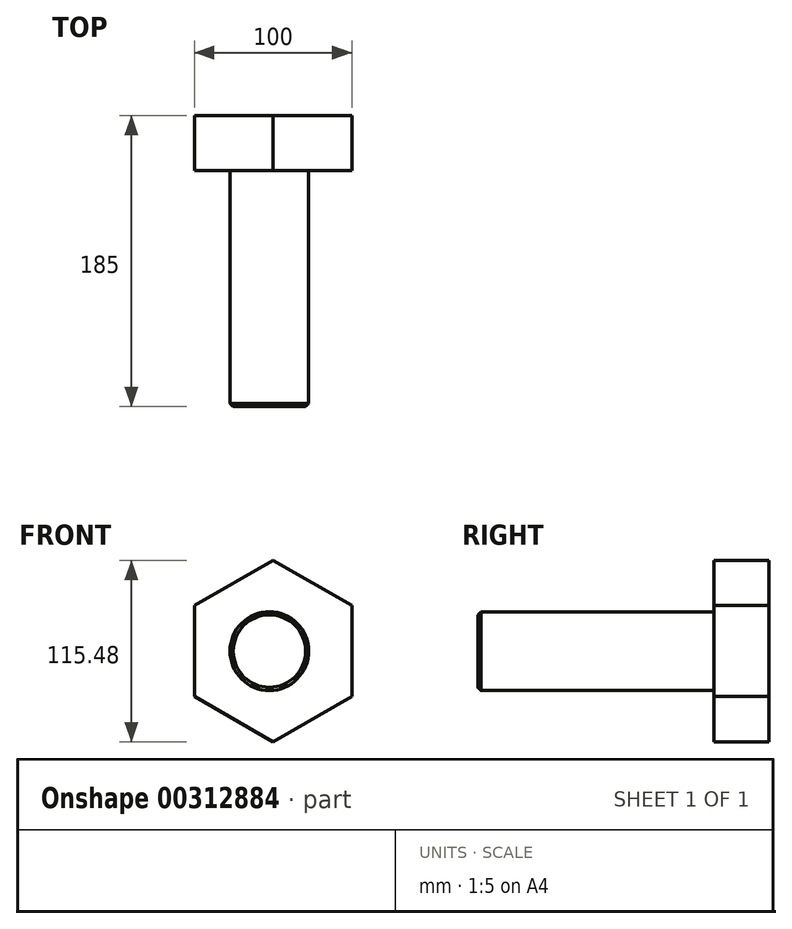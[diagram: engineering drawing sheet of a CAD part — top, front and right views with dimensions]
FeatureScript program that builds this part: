
annotation { "Feature Type Name" : "Feature", "Feature Type Description" : "" }
export const myFeature = defineFeature(function(context is Context, id is Id, definition is map)
    precondition{}
    {
        {
            var Q0;
            Q0=qCreatedBy(makeId("Front.planeOp"),FACE);
            var sketch = newSketch(context, id + "F0", { "sketchPlane" : qUnion([Q0])});
            skCircle(sketch, "E0.cCircle", {"center": v(2.35, 0) * mm, "radius": 50 * mm, "construction": true});
            skLineSegment(sketch, "E0.0", {"start": v(52.35, 28.87) * mm, "end": v(52.35, -28.87) * mm});
            skLineSegment(sketch, "E0.1", {"start": v(52.35, -28.87) * mm, "end": v(2.35, -57.74) * mm});
            skLineSegment(sketch, "E0.2", {"start": v(2.35, -57.74) * mm, "end": v(-47.65, -28.87) * mm});
            skLineSegment(sketch, "E0.3", {"start": v(-47.65, -28.87) * mm, "end": v(-47.65, 28.87) * mm});
            skLineSegment(sketch, "E0.4", {"start": v(-47.65, 28.87) * mm, "end": v(2.35, 57.74) * mm});
            skLineSegment(sketch, "E0.5", {"start": v(2.35, 57.74) * mm, "end": v(52.35, 28.87) * mm});
            skPoint(sketch, "E0.0.midPoint", {"position": v(52.35, 0) * mm});
            skSolve(sketch);
        }
        {
            var Q0;
            Q0=makeQuery(id+"F0.imprint","IMPRINT",FACE,{"disambiguationData":[TD([[makeQuery(id+"F0.imprint","IMPRINT",EDGE,{"derivedFrom":sQuery(id+"F0.wireOp",EDGE,"E0.0")}),-1.0]])]});
            extrude(context, id + "F1", {"entities" : qUnion([Q0]), "depth" : 35 * mm});
        }
        {
            var Q0;
            Q0=makeQuery(id+"F1.opExtrude","CAP_FACE",FACE,{"disambiguationData":[OSD([sQuery(id+"F0.wireOp",EDGE,"E0.0"),sQuery(id+"F0.wireOp",EDGE,"E0.1"),sQuery(id+"F0.wireOp",EDGE,"E0.2"),sQuery(id+"F0.wireOp",EDGE,"E0.3"),sQuery(id+"F0.wireOp",EDGE,"E0.4"),sQuery(id+"F0.wireOp",EDGE,"E0.5")])],"isStart":false});
            var sketch = newSketch(context, id + "F2", { "sketchPlane" : qUnion([Q0])});
            skCircle(sketch, "E1", {"center": v(0, 0) * mm, "radius": 25 * mm});
            skSolve(sketch);
        }
        {
            var Q0;
            Q0=makeQuery(id+"F2.imprint","IMPRINT",FACE,{"disambiguationData":[TD([[makeQuery(id+"F2.imprint","IMPRINT",EDGE,{"derivedFrom":sQuery(id+"F2.wireOp",EDGE,"E1")}),1.0]])]});
            extrude(context, id + "F3", {"entities" : qUnion([Q0]), "operationType" : NewBodyOperationType.ADD, "depth" : 150 * mm});
        }
        {
            var Q0;
            Q0=makeQuery(id+"F3.opExtrude","CAP_EDGE",EDGE,{"disambiguationData":[OSD([sQuery(id+"F2.wireOp",EDGE,"E1")])],"isStart":false});
            chamfer(context, id + "F4", {"entities" : qUnion([Q0]), "width" : 2 * mm, "tangentPropagation" : true});
        }
    });
